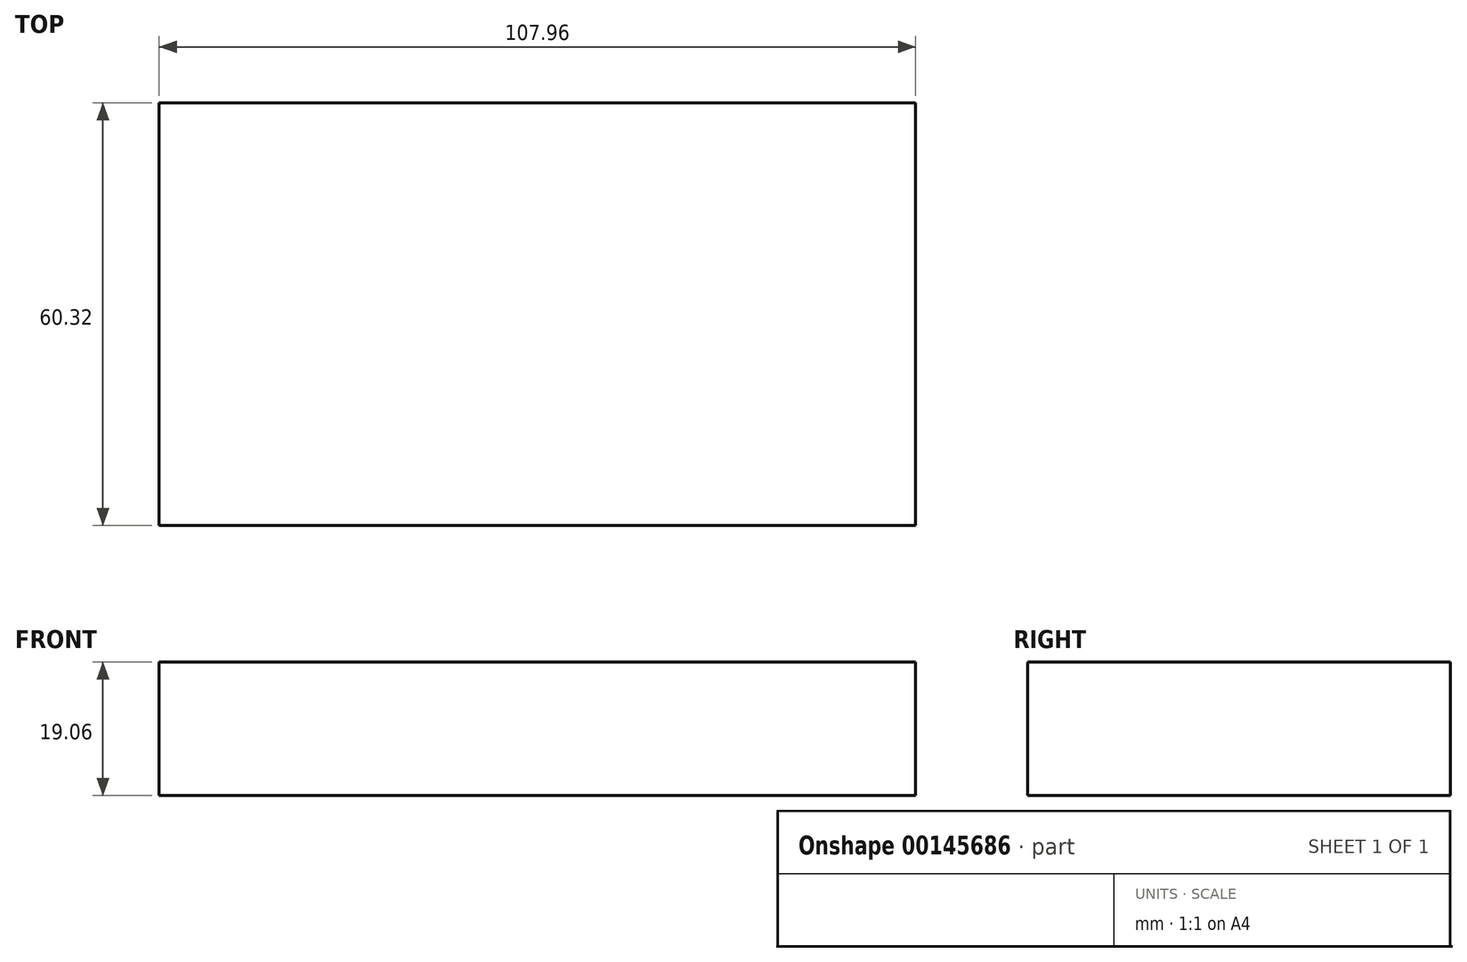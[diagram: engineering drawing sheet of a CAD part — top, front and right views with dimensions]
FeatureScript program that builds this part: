
annotation { "Feature Type Name" : "Feature", "Feature Type Description" : "" }
export const myFeature = defineFeature(function(context is Context, id is Id, definition is map)
    precondition{}
    {
        {
            var Q0;
            Q0=qCreatedBy(makeId("Front.planeOp"),FACE);
            var sketch = newSketch(context, id + "F0", { "sketchPlane" : qUnion([Q0])});
            skLineSegment(sketch, "E0.bottom", {"start": v(53.98, 9.53) * mm, "end": v(-53.98, 9.53) * mm});
            skLineSegment(sketch, "E0.top", {"start": v(53.98, -9.53) * mm, "end": v(-53.98, -9.53) * mm});
            skLineSegment(sketch, "E0.left", {"start": v(53.98, 9.53) * mm, "end": v(53.98, -9.52) * mm});
            skLineSegment(sketch, "E0.right", {"start": v(-53.98, 9.53) * mm, "end": v(-53.98, -9.53) * mm});
            skPoint(sketch, "E0.middle", {"position": v(0, 0) * mm});
            skSolve(sketch);
        }
        {
            var Q0;
            Q0 = qSketchRegion(id + "F0", true);
            extrude(context, id + "F1", {"entities" : qUnion([Q0]), "depth" : 60.32 * mm});
        }
    });
